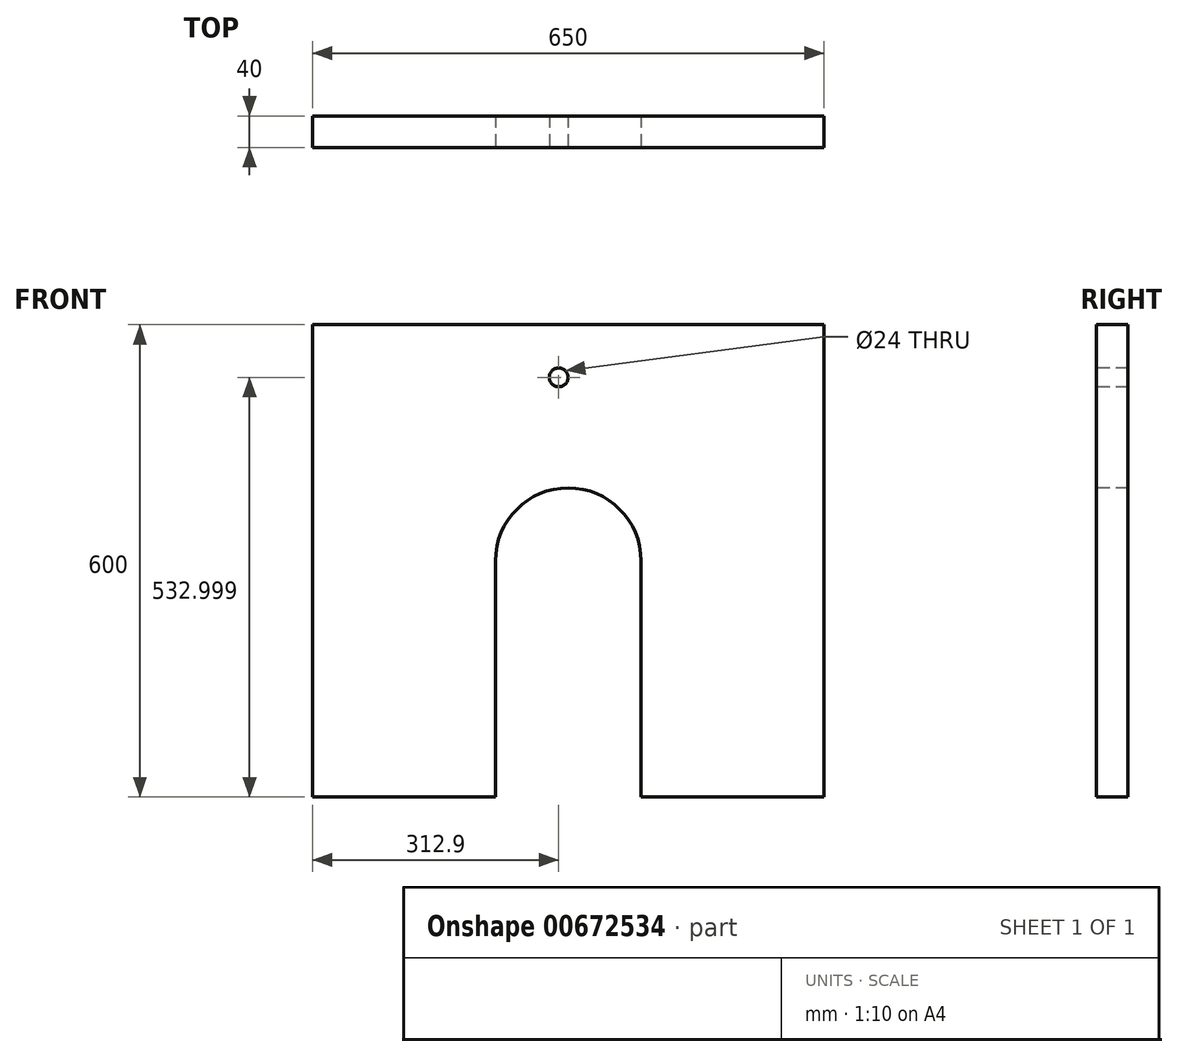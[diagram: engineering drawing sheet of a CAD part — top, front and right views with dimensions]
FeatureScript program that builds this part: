
annotation { "Feature Type Name" : "Feature", "Feature Type Description" : "" }
export const myFeature = defineFeature(function(context is Context, id is Id, definition is map)
    precondition{}
    {
        {
            var Q0;
            Q0=qCreatedBy(makeId("Front.planeOp"),FACE);
            var sketch = newSketch(context, id + "F0", { "sketchPlane" : qUnion([Q0])});
            skLineSegment(sketch, "E0.bottom", {"start": v(-312.9, 279.46) * mm, "end": v(337.1, 279.46) * mm});
            skLineSegment(sketch, "E0.top", {"start": v(-312.9, -320.54) * mm, "end": v(337.1, -320.54) * mm});
            skLineSegment(sketch, "E0.left", {"start": v(-312.9, 279.46) * mm, "end": v(-312.9, -320.54) * mm});
            skLineSegment(sketch, "E0.right", {"start": v(337.1, 279.46) * mm, "end": v(337.1, -320.54) * mm});
            skSolve(sketch);
        }
        {
            var Q0;
            Q0 = qSketchRegion(id + "F0", true);
            extrude(context, id + "F1", {"entities" : qUnion([Q0]), "depth" : 40 * mm, "offsetDistance" : 25 * mm});
        }
        {
            var Q0;
            Q0=makeQuery(id+"F1.opExtrude","CAP_FACE",FACE,{"disambiguationData":[OSD([sQuery(id+"F0.wireOp",EDGE,"E0.bottom"),sQuery(id+"F0.wireOp",EDGE,"E0.top"),sQuery(id+"F0.wireOp",EDGE,"E0.left"),sQuery(id+"F0.wireOp",EDGE,"E0.right")])],"isStart":false});
            var sketch = newSketch(context, id + "F2", { "sketchPlane" : qUnion([Q0])});
            skLineSegment(sketch, "E1", {"start": v(-80.4, -320.54) * mm, "end": v(-80.4, -20.54) * mm});
            skLineSegment(sketch, "E2", {"start": v(104.6, -20.54) * mm, "end": v(104.6, -320.54) * mm});
            skArc(sketch, "E3", {"start": v(104.6, -20.54) * mm, "mid": v(12.1, 71.96) * mm, "end": v(-80.4, -20.54) * mm});
            skLineSegment(sketch, "E4", {"start": v(-80.4, -320.54) * mm, "end": v(104.6, -320.54) * mm});
            skSolve(sketch);
        }
        {
            var Q0;
            Q0 = qSketchRegion(id + "F2", true);
            extrude(context, id + "F3", {"entities" : qUnion([Q0]), "operationType" : NewBodyOperationType.REMOVE, "endBound" : BoundingType.THROUGH_ALL, "oppositeDirection" : true, "depth" : 25 * mm, "offsetDistance" : 25 * mm});
        }
        {
            var Q0;
            Q0=makeQuery(id+"F1.opExtrude","CAP_FACE",FACE,{"disambiguationData":[OSD([sQuery(id+"F0.wireOp",EDGE,"E0.bottom"),sQuery(id+"F0.wireOp",EDGE,"E0.top"),sQuery(id+"F0.wireOp",EDGE,"E0.left"),sQuery(id+"F0.wireOp",EDGE,"E0.right")])],"isStart":false});
            var sketch = newSketch(context, id + "F4", { "sketchPlane" : qUnion([Q0])});
            skCircle(sketch, "E5", {"center": v(0, 212.46) * mm, "radius": 12 * mm});
            skSolve(sketch);
        }
        {
            var Q0;
            Q0 = qSketchRegion(id + "F4", true);
            extrude(context, id + "F5", {"entities" : qUnion([Q0]), "operationType" : NewBodyOperationType.REMOVE, "endBound" : BoundingType.THROUGH_ALL, "oppositeDirection" : true, "depth" : 25 * mm, "offsetDistance" : 25 * mm});
        }
        {
            var Q0;
            Q0=qCreatedBy(makeId("Right.planeOp"),FACE);
            var sketch = newSketch(context, id + "F6", { "sketchPlane" : qUnion([Q0])});
            skLineSegment(sketch, "E6", {"start": v(264.22, -20.54) * mm, "end": v(-302.22, -20.54) * mm});
            skSolve(sketch);
        }
    });
